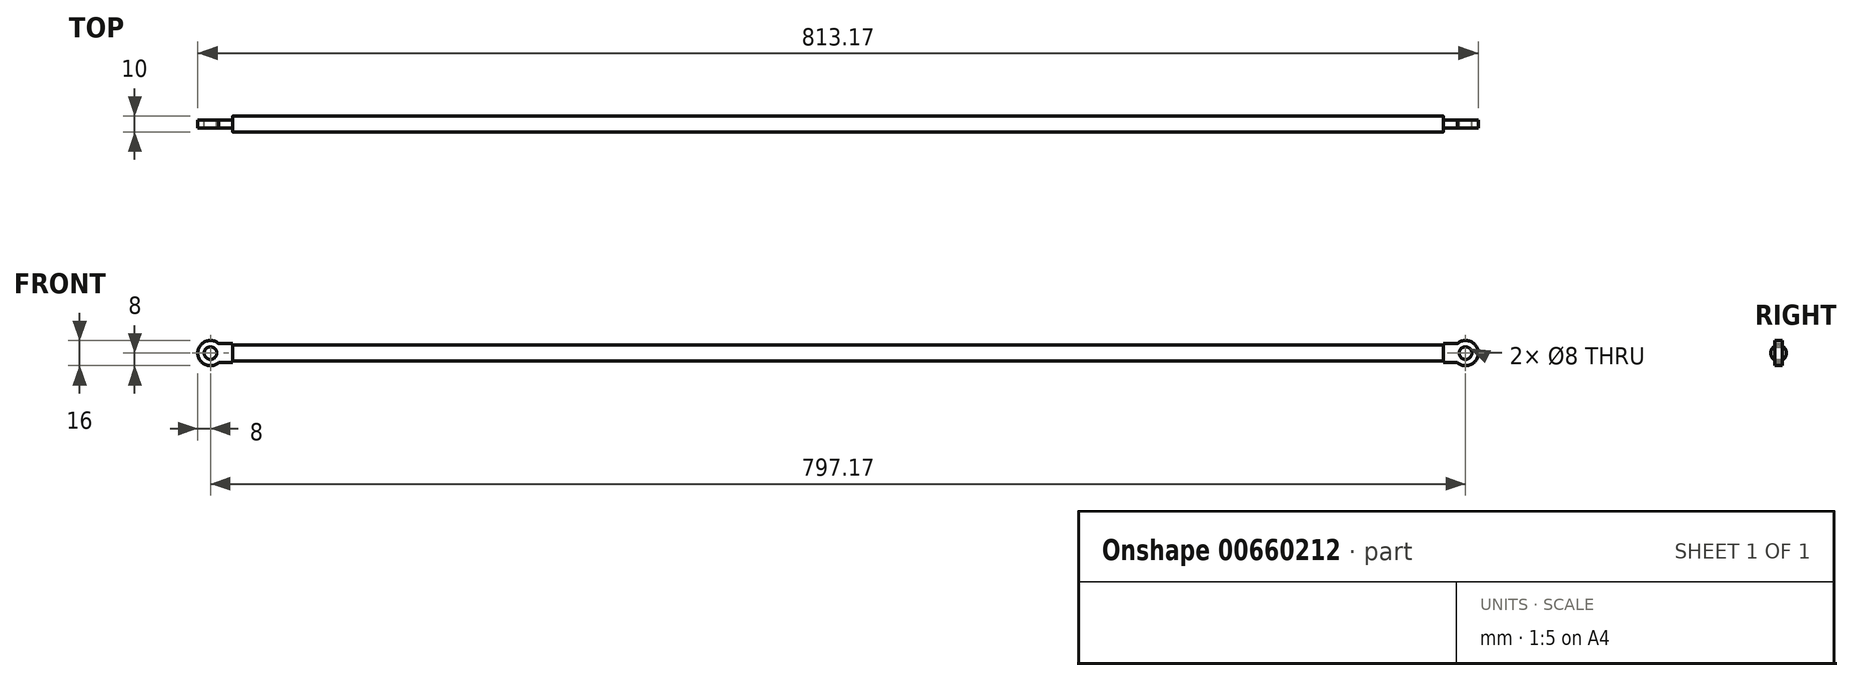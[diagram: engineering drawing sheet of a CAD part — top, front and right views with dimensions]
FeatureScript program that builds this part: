
annotation { "Feature Type Name" : "Feature", "Feature Type Description" : "" }
export const myFeature = defineFeature(function(context is Context, id is Id, definition is map)
    precondition{}
    {
        {
            var Q0;
            Q0=qCreatedBy(makeId("Right.planeOp"),FACE);
            var sketch = newSketch(context, id + "F0", { "sketchPlane" : qUnion([Q0])});
            skCircle(sketch, "E0", {"center": v(0, 0) * mm, "radius": 5 * mm});
            skSolve(sketch);
        }
        {
            var Q0;
            Q0=qSketchRegion(id+"F0",true);
            extrude(context, id + "F1", {"entities" : qUnion([Q0]), "depth" : 769.17 * mm, "offsetDistance" : 25 * mm});
        }
        {
            var Q0;
            Q0=qCreatedBy(makeId("Front.planeOp"),FACE);
            var sketch = newSketch(context, id + "F2", { "sketchPlane" : qUnion([Q0])});
            skLineSegment(sketch, "E1.bottom", {"start": v(0, 6) * mm, "end": v(-8.7, 6) * mm});
            skLineSegment(sketch, "E1.top", {"start": v(0, -6) * mm, "end": v(-8.7, -6) * mm});
            skLineSegment(sketch, "E1.left", {"start": v(0, 6) * mm, "end": v(0, -6) * mm});
            skCircle(sketch, "E2", {"center": v(-14, 0) * mm, "radius": 4 * mm});
            skArc(sketch, "E3", {"start": v(-8.7, 6) * mm, "mid": v(-22, 0) * mm, "end": v(-8.7, -6) * mm});
            skLineSegment(sketch, "E4", {"start": v(384.59, 48.86) * mm, "end": v(384.59, -63.28) * mm, "construction": true});
            skLineSegment(sketch, "E5.MirrorCS", {"start": v(769.17, 6) * mm, "end": v(769.17, -6) * mm});
            skLineSegment(sketch, "E6.MirrorCS", {"start": v(769.17, -6) * mm, "end": v(777.88, -6) * mm});
            skLineSegment(sketch, "E7.MirrorCS", {"start": v(769.17, 6) * mm, "end": v(777.88, 6) * mm});
            skArc(sketch, "E8.MirrorCS", {"start": v(777.88, 6) * mm, "mid": v(791.17, 0) * mm, "end": v(777.88, -6) * mm});
            skCircle(sketch, "E9.MirrorC", {"center": v(783.17, 0) * mm, "radius": 4 * mm});
            skSolve(sketch);
        }
        {
            var Q0;
            Q0=qSketchRegion(id+"F2",true);
            extrude(context, id + "F3", {"entities" : qUnion([Q0]), "operationType" : NewBodyOperationType.ADD, "endBound" : BoundingType.SYMMETRIC, "depth" : 5 * mm, "offsetDistance" : 25 * mm});
        }
    });
